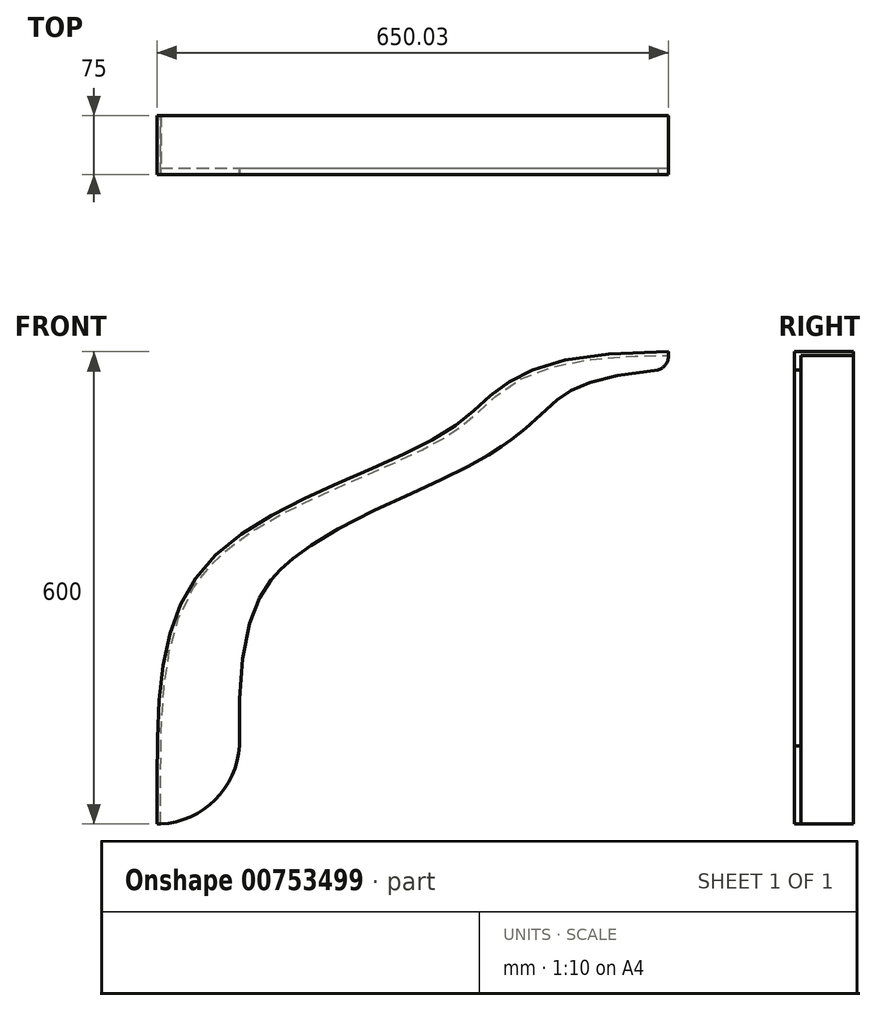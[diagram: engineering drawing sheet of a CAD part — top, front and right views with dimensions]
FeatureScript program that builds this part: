
annotation { "Feature Type Name" : "Feature", "Feature Type Description" : "" }
export const myFeature = defineFeature(function(context is Context, id is Id, definition is map)
    precondition{}
    {
        {
            var Q0;
            Q0=qCreatedBy(makeId("Front.planeOp"),FACE);
            var sketch = newSketch(context, id + "F0", { "sketchPlane" : qUnion([Q0])});
            skFitSpline(sketch, "E0", {"points": [v(0, 0) * mm, v(71.5, 338.84) * mm, v(371.67, 500.85) * mm, v(650, 600) * mm], "startDerivative": vector(0, 1338.95) * mm, "endDerivative": vector(2001.6, 0) * mm});
            skFitSpline(sketch, "E1.0", {"points": [v(5, 0) * mm, v(5, 27.9) * mm, v(4.75, 80.87) * mm, v(6.32, 140.06) * mm, v(10.18, 183.28) * mm, v(14.74, 213.65) * mm, v(21.32, 241.99) * mm, v(30.26, 268.34) * mm, v(41.93, 292.76) * mm, v(54.22, 311.56) * mm, v(65.8, 325.72) * mm, v(75.4, 335.9) * mm, v(85.98, 345.67) * mm, v(101.32, 358.2) * mm, v(122.53, 372.96) * mm, v(150.52, 389.4) * mm, v(180.32, 404.74) * mm, v(211.18, 419.17) * mm, v(242.37, 432.9) * mm, v(273.15, 446.13) * mm, v(302.8, 459.08) * mm, v(325.98, 469.8) * mm, v(343.23, 478.47) * mm, v(355.45, 485.04) * mm, v(364.96, 490.6) * mm, v(372.11, 495.13) * mm, v(378.95, 499.7) * mm, v(386.88, 505.5) * mm, v(395.6, 512.48) * mm, v(403.72, 519.46) * mm, v(414.02, 528.66) * mm, v(426.38, 539.86) * mm, v(442.03, 552.46) * mm, v(460.13, 564) * mm, v(482.45, 574.27) * mm, v(510.74, 582.94) * mm, v(546.66, 589.63) * mm, v(591.86, 593.96) * mm, v(629.23, 595) * mm, v(650, 595) * mm]});
            skLineSegment(sketch, "E2", {"start": v(650, 600) * mm, "end": v(650, 595) * mm});
            skLineSegment(sketch, "E3", {"start": v(0, 0) * mm, "end": v(5, 0) * mm});
            skSolve(sketch);
        }
        {
            var Q0;
            Q0 = qSketchRegion(id + "F0", true);
            extrude(context, id + "F1", {"entities" : qUnion([Q0]), "depth" : 75 * mm, "offsetDistance" : 25 * mm});
        }
        {
            var Q0;
            Q0=makeQuery(id+"F1.opExtrude","CAP_FACE",FACE,{"disambiguationData":[OSD([sQuery(id+"F0.wireOp",EDGE,"E0"),sQuery(id+"F0.wireOp",EDGE,"E1.0"),sQuery(id+"F0.wireOp",EDGE,"E2"),sQuery(id+"F0.wireOp",EDGE,"E3")])],"isStart":false});
            var sketch = newSketch(context, id + "F2", { "sketchPlane" : qUnion([Q0])});
            skFitSpline(sketch, "E4.0", {"points": [v(5, 0) * mm, v(5, 27.9) * mm, v(4.75, 80.87) * mm, v(6.32, 140.06) * mm, v(10.18, 183.28) * mm, v(14.74, 213.65) * mm, v(21.32, 241.99) * mm, v(30.26, 268.34) * mm, v(41.93, 292.76) * mm, v(54.22, 311.56) * mm, v(65.8, 325.72) * mm, v(75.4, 335.9) * mm, v(85.98, 345.67) * mm, v(101.32, 358.2) * mm, v(122.53, 372.96) * mm, v(150.52, 389.4) * mm, v(180.32, 404.74) * mm, v(211.18, 419.17) * mm, v(242.37, 432.9) * mm, v(273.15, 446.13) * mm, v(302.8, 459.08) * mm, v(325.98, 469.8) * mm, v(343.23, 478.47) * mm, v(355.45, 485.04) * mm, v(364.96, 490.6) * mm, v(372.11, 495.13) * mm, v(378.95, 499.7) * mm, v(386.88, 505.5) * mm, v(395.6, 512.48) * mm, v(403.72, 519.46) * mm, v(414.02, 528.66) * mm, v(426.38, 539.86) * mm, v(442.03, 552.46) * mm, v(460.13, 564) * mm, v(482.45, 574.27) * mm, v(510.74, 582.94) * mm, v(546.66, 589.63) * mm, v(591.86, 593.96) * mm, v(629.23, 595) * mm, v(650, 595) * mm]});
            skFitSpline(sketch, "E5.0", {"points": [v(106.75, 20.17) * mm, v(106.1, 48.23) * mm, v(105.03, 87.73) * mm, v(104.81, 135.08) * mm, v(105.59, 167.84) * mm, v(107.59, 197.77) * mm, v(111.04, 224.8) * mm, v(116.1, 248.92) * mm, v(121.7, 266.68) * mm, v(127.08, 279.65) * mm, v(131.6, 288.83) * mm, v(136.61, 297.54) * mm, v(141.28, 304.47) * mm, v(145.34, 309.87) * mm, v(148.56, 313.85) * mm, v(151.4, 317.11) * mm, v(153.77, 319.7) * mm, v(155.6, 321.63) * mm, v(157.5, 323.56) * mm, v(160.14, 326.15) * mm, v(163.6, 329.4) * mm, v(168.04, 333.3) * mm, v(172.74, 337.23) * mm, v(177.7, 341.15) * mm, v(184.66, 346.37) * mm, v(193.94, 352.87) * mm, v(205.93, 360.6) * mm, v(222.92, 370.78) * mm, v(245.77, 383.21) * mm, v(274.95, 397.69) * mm, v(305.1, 411.79) * mm, v(330.43, 423.36) * mm, v(350.47, 432.62) * mm, v(365.32, 439.6) * mm, v(379.9, 446.66) * mm, v(394.16, 453.84) * mm, v(405.72, 459.97) * mm, v(414.76, 465.01) * mm, v(421.42, 468.87) * mm, v(426.88, 472.16) * mm, v(431.19, 474.85) * mm, v(434.38, 476.9) * mm, v(437.02, 478.63) * mm, v(439.12, 480.03) * mm, v(440.7, 481.1) * mm, v(442.25, 482.17) * mm, v(444.3, 483.6) * mm, v(446.83, 485.4) * mm, v(449.8, 487.58) * mm, v(453.64, 490.47) * mm, v(458.23, 494.06) * mm, v(463.43, 498.33) * mm, v(468.34, 502.52) * mm, v(472.97, 506.61) * mm, v(478.8, 511.9) * mm, v(485.48, 518.16) * mm, v(492.7, 524.97) * mm, v(499.3, 531.05) * mm, v(505.5, 536.42) * mm, v(511.53, 541.2) * mm, v(516.64, 544.82) * mm, v(520.96, 547.58) * mm, v(524.36, 549.6) * mm, v(527.98, 551.57) * mm, v(533.14, 554.17) * mm, v(540.36, 557.36) * mm, v(550.61, 561.1) * mm, v(562.78, 564.7) * mm, v(577.11, 568.09) * mm, v(599.44, 572.18) * mm, v(633.85, 576.3) * mm, v(669.29, 578.1) * mm, v(689.2, 578.55) * mm]});
            skArc(sketch, "E6", {"start": v(0, 0) * mm, "mid": v(74.6, 31.11) * mm, "end": v(105, 106) * mm});
            skArc(sketch, "E7", {"start": v(632.22, 575.62) * mm, "mid": v(644.88, 581.85) * mm, "end": v(650, 595) * mm});
            skSolve(sketch);
        }
        {
            var Q0;
            Q0 = qSketchRegion(id + "F2", true);
            extrude(context, id + "F3", {"entities" : qUnion([Q0]), "operationType" : NewBodyOperationType.ADD, "oppositeDirection" : true, "depth" : 8 * mm, "offsetDistance" : 25 * mm});
        }
    });
